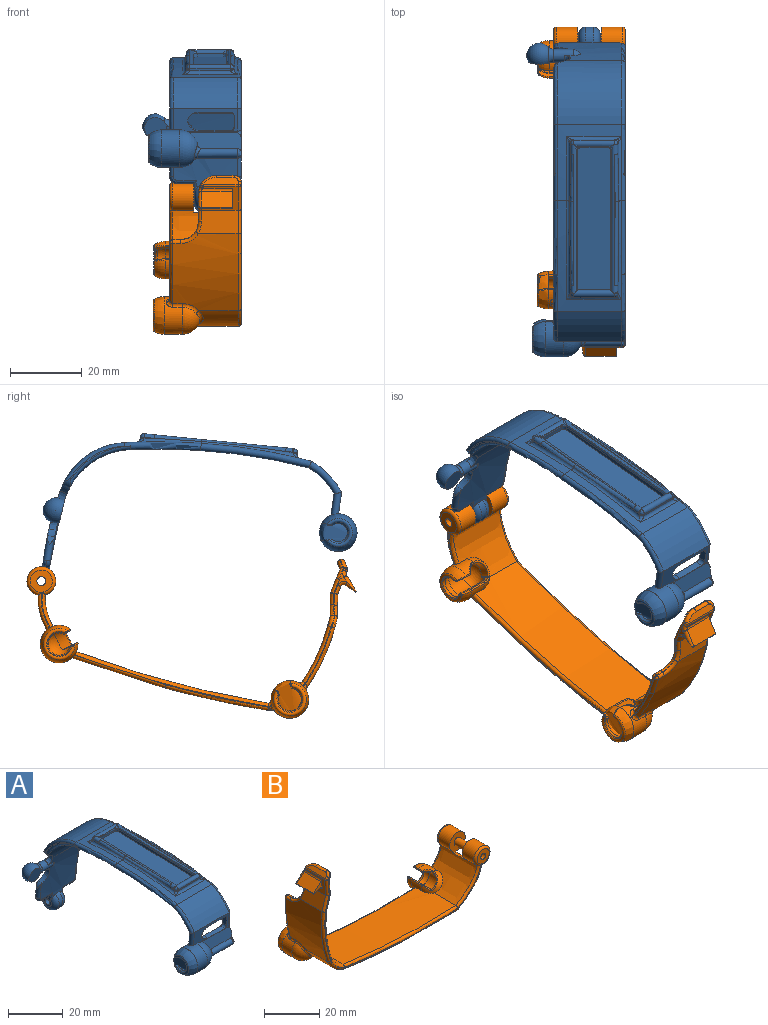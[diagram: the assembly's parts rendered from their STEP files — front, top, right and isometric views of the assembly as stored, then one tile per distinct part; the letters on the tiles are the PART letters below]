
ASSEMBLY  parts=2 mates=1
PART A: 147 faces, bbox 30.4x94.3x50.8 mm
  f0: plane 36.93x1.25mm, normal (0,-0.03,1), area 5.1mm2, adj f125,f126,f127
  f1: plane 2.82x0.31mm, normal (1,0,0), area 0.4mm2, adj f113,f123,f136
  f2: plane 2.24x0.34mm, normal (-1,0,0), area 0.3mm2, adj f112,f126,f129
  f3: torus R=90.74mm, axis (1,0,0), area 17.7mm2, adj f4,f22,f74,f76,f97
  f4: cylinder r=89.74mm len=21.05mm, axis (-1,0,0), area 314.4mm2, adj f3,f6,f13,f65,f67,f68,f75,f76
  f5: cylinder r=20mm len=18mm, axis (-1,0,0), area 420.5mm2, adj f7,f22,f23,f66,f94,f95
  f6: cylinder r=20mm len=18mm, axis (1,0,0), area 425.5mm2, adj f4,f8,f28,f64,f94,f95,f96
  f7: torus R=19mm, axis (1,0,0), area 31.9mm2, adj f5,f19,f73,f94
  f8: torus R=21mm, axis (1,0,0), area 31.6mm2, adj f6,f19,f73,f94
  f9: torus R=2mm, axis (1,0,0), area 2.1mm2, adj f10,f11,f20,f29,f60
  f10: cylinder r=1mm len=6.94mm, axis (0,0.08,-1), area 19.6mm2, adj f9,f11,f17,f18,f59,f61
  f11: plane 0.58x0.06mm, normal (1,0,0), area 0mm2, adj f9,f10,f59
  f12: plane 18.1x15.35mm, normal (1,0,0), area 6.5mm2, adj f63,f64,f65,f66
  f13: cylinder r=4mm len=8mm, axis (-1,0,0), area 46.1mm2, adj f4,f22,f83,f84
  f14: sphere r=3.75mm, area 55.4mm2, adj f35,f37,f38
  f15: cylinder r=1.3mm len=11.27mm, axis (-1,0,0), area 43.9mm2, adj f16,f20,f57,f77
  f16: cylinder r=1.8mm len=11.38mm, axis (-1,0,0), area 28.9mm2, adj f15,f21,f58,f77
  f17: plane 18.02x6.38mm, normal (0,-1,-0.08), area 48.4mm2, adj f10,f25,f30,f31,f39,f41,f42,f60
  f18: plane 18.02x6.15mm, normal (0,1,0.08), area 43.8mm2, adj f10,f21,f26,f30,f31,f39,f40,f41
  f19: plane 16.22x10.31mm, normal (-1,0,0), area 5.9mm2, adj f7,f8,f73,f94
  f20: plane 17.67x8.45mm, normal (0,-0.98,0.21), area 59.6mm2, adj f9,f15,f29,f30,f57,f60,f77
  f21: plane 15.46x6.4mm, normal (0,0.98,-0.21), area 77.7mm2, adj f16,f18,f30,f59,f77
  f22: cylinder r=91.74mm len=22.56mm, axis (-1,0,0), area 338.7mm2, adj f3,f5,f13,f65,f68,f69,f74,f75
  f23: cylinder r=192.82mm len=21.29mm, axis (-1,0,0), area 109.1mm2, adj f5,f24,f63,f73,f113,f114,f115
  f24: cylinder r=165.2mm len=31.08mm, axis (-1,0,0), area 136.2mm2, adj f23,f25,f62,f72,f110,f111,f112
  f25: cylinder r=22mm len=18mm, axis (-1,0,0), area 220.3mm2, adj f17,f24,f61,f71
  f26: cylinder r=20mm len=18mm, axis (-1,0,0), area 184mm2, adj f18,f27,f61,f71
  f27: cylinder r=163.2mm len=30.43mm, axis (-1,0,0), area 550.9mm2, adj f26,f28,f62,f72
  f28: cylinder r=190.82mm len=19.58mm, axis (-1,0,0), area 353.1mm2, adj f6,f27,f63,f73
  f29: plane 7.23x3.75mm, normal (1,0,0), area 5.1mm2, adj f9,f20,f57,f58,f59
  f30: sphere r=5.25mm, area 114.2mm2, adj f17,f18,f20,f21,f31,f51,f52,f60
  f31: cylinder r=5.25mm len=10.5mm, axis (-1,0,0), area 130.2mm2, adj f17,f18,f30,f32,f49,f50,f53,f70
  f32: revolved ~10.48x10.02mm, area 94mm2, adj f31,f45,f48,f54
  f33: cone r=3.42mm half-angle=35.3deg, axis (-1,0,0), area 10.2mm2, adj f34,f45,f46,f56
  f34: sphere r=3.75mm, area 52.2mm2, adj f33,f35,f36,f38,f46,f56
  f35: cylinder r=3.75mm len=7.5mm, axis (1,0,0), area 91.7mm2, adj f14,f34,f36,f37,f38
  f36: plane 5.15x2.64mm, normal (0,-0.04,-1), area 6.5mm2, adj f34,f35,f37,f46,f47,f48,f49
  f37: cylinder r=3.75mm len=6.95mm, axis (0,-1,0.04), area 29.1mm2, adj f14,f35,f36,f38,f49,f50,f51
  f38: plane 11.67x4.47mm, normal (0,0.04,1), area 15mm2, adj f14,f34,f35,f37,f51,f52,f53,f54
  f39: plane 2.02x0.45mm, normal (0.64,-0.06,0.77), area 0.9mm2, adj f17,f18,f80,f81
  f40: plane 8.64x2mm, normal (0,-0.08,1), area 17.4mm2, adj f18,f60,f78,f80
  f41: plane 3.64x2.26mm, normal (-1,0,0), area 7mm2, adj f17,f18,f78,f79
  f42: plane 9x1.99mm, normal (0,0.08,-1), area 18mm2, adj f17,f18,f79,f82
  f43: plane 6.03x4mm, normal (1,0,0), area 9.9mm2, adj f68,f84,f85,f86,f88
  f44: plane 6.03x4mm, normal (-1,0,0), area 9.9mm2, adj f75,f83,f85,f87,f89
  f45: torus R=3.5mm, axis (1,0,0), area 18.5mm2, adj f32,f33,f47,f55
  f46: bspline ~1.96x1.9mm, area 0.2mm2, adj f33,f34,f36,f47
  f47: bspline ~1.27x0.49mm, area 0.4mm2, adj f36,f45,f46,f48
  f48: bspline ~5.35x2.73mm, area 2.4mm2, adj f32,f36,f47,f49
  f49: cylinder r=0.3mm len=1.81mm, axis (-1,0,0), area 1.1mm2, adj f31,f36,f37,f48,f50
  f50: bspline ~4.25x2.57mm, area 2.8mm2, adj f31,f37,f49,f51
  f51: torus R=4.05mm, axis (0,-1,0.04), area 6.3mm2, adj f30,f37,f38,f50,f52
  f52: torus R=4.46mm, axis (0,0.04,1), area 2.4mm2, adj f30,f38,f51,f53
  f53: cylinder r=0.3mm len=5mm, axis (-1,0,0), area 3mm2, adj f31,f38,f52,f54
  f54: bspline ~5.37x2.69mm, area 2.3mm2, adj f32,f38,f53,f55
  f55: bspline ~1.27x0.49mm, area 0.4mm2, adj f38,f45,f54,f56
  f56: bspline ~1.99x1.88mm, area 0.2mm2, adj f33,f34,f38,f55
  f57: torus R=0.3mm, axis (1,0,0), area 2.9mm2, adj f15,f20,f29,f58
  f58: torus R=0.8mm, axis (1,0,0), area 3.2mm2, adj f16,f29,f57,f59
  f59: cylinder r=1mm len=6.55mm, axis (0,-0.21,-0.98), area 9.9mm2, adj f10,f11,f21,f29,f58
  f60: cylinder r=1mm len=14.43mm, axis (1,0,0), area 2.8mm2, adj f9,f17,f20,f30,f40,f78,f80
  f61: torus R=21mm, axis (1,0,0), area 35.3mm2, adj f10,f25,f26,f62
  f62: torus R=164.2mm, axis (1,0,0), area 97.2mm2, adj f24,f27,f61,f63
  f63: torus R=191.82mm, axis (1,0,0), area 64.3mm2, adj f12,f23,f28,f62,f64,f66
  f64: torus R=21mm, axis (1,0,0), area 38.4mm2, adj f6,f12,f63,f65
  f65: torus R=90.74mm, axis (1,0,0), area 60.4mm2, adj f4,f12,f22,f64,f66,f67,f69
  f66: torus R=19mm, axis (1,0,0), area 36.2mm2, adj f5,f12,f63,f65
  f67: bspline ~2.7x2.49mm, area 4.4mm2, adj f4,f65,f68,f69
  f68: cylinder r=1mm len=5.5mm, axis (-1,0,0), area 16.2mm2, adj f4,f22,f43,f67,f69,f86,f88
  f69: bspline ~2.5x2.45mm, area 3.7mm2, adj f22,f65,f67,f68
  f70: cylinder r=1mm len=6.86mm, axis (0,0.08,-1), area 18.8mm2, adj f17,f18,f31,f71
  f71: torus R=21mm, axis (1,0,0), area 35.3mm2, adj f25,f26,f70,f72
  f72: torus R=164.2mm, axis (1,0,0), area 97.2mm2, adj f24,f27,f71,f73
  f73: torus R=191.82mm, axis (1,0,0), area 64.3mm2, adj f7,f8,f19,f23,f28,f72
  f74: bspline ~2.5x2.12mm, area 3.7mm2, adj f3,f22,f75,f76
  f75: cylinder r=1mm len=5.5mm, axis (1,0,0), area 16.2mm2, adj f4,f22,f44,f74,f76,f87,f89
  f76: bspline ~2.7x2.49mm, area 4.4mm2, adj f3,f4,f74,f75
  f77: bspline ~3.87x3.87mm, area 6.3mm2, adj f15,f16,f20,f21,f30
  f78: cylinder r=1mm len=2.08mm, axis (0,-1,-0.08), area 3.1mm2, adj f17,f18,f40,f41,f60
  f79: cylinder r=1mm len=2.07mm, axis (0,1,0.08), area 3.1mm2, adj f17,f18,f41,f42
  f80: cylinder r=3mm len=2.06mm, axis (0,1,0.08), area 4.2mm2, adj f17,f18,f39,f40,f60
  f81: cylinder r=3mm len=2.14mm, axis (0,1,0.08), area 4.5mm2, adj f17,f18,f39,f82
  f82: cylinder r=3mm len=2.97mm, axis (0,-1,-0.08), area 8.6mm2, adj f17,f18,f42,f81
  f83: torus R=2mm, axis (-1,0,0), area 58.5mm2, adj f4,f13,f22,f44,f87,f89
  f84: torus R=2mm, axis (1,0,0), area 58.5mm2, adj f4,f13,f22,f43,f86,f88
  f85: cylinder r=1.25mm len=6mm, axis (-1,0,0), area 47.1mm2, adj f43,f44
  f86: torus R=90.24mm, axis (1,0,0), area 1.9mm2, adj f4,f43,f68,f84
  f87: torus R=90.24mm, axis (-1,0,0), area 1.9mm2, adj f4,f44,f75,f83
  f88: torus R=91.24mm, axis (1,0,0), area 1.5mm2, adj f22,f43,f68,f84
  f89: torus R=91.24mm, axis (-1,0,0), area 1.5mm2, adj f22,f44,f75,f83
  f90: revolved ~3.38x2.08mm, area 7mm2, adj f22,f91
  f91: cylinder r=1.8mm len=6.5mm, axis (1,0,0), area 51.9mm2, adj f4,f22,f90,f92,f96,f98,f144,f145
  f92: revolved ~1.93x0.55mm, area 0mm2, adj f4,f91
  f93: sphere r=3.5mm, area 99.9mm2, adj f145,f146
  f94: torus R=9.76mm, axis (1,0,0), area 4.5mm2, adj f5,f6,f7,f8,f19,f95
  f95: torus R=1.3mm, axis (1,0,0), area 6.8mm2, adj f5,f6,f22,f94,f96
  f96: revolved ~5.43x4.87mm, area 10.5mm2, adj f4,f6,f22,f91,f95
  f97: torus R=9.76mm, axis (1,0,0), area 4.1mm2, adj f3,f4,f22,f99
  f98: revolved ~6.43x4.21mm, area 11.4mm2, adj f4,f22,f91,f99
  f99: torus R=1.3mm, axis (1,0,0), area 6.6mm2, adj f4,f22,f97,f98
  f100: plane 11.32x0.55mm, normal (0,1,0.03), area 6.3mm2, adj f115,f124,f135,f136,f141,f142
  f101: plane 7.29x1mm, normal (0,-1,-0.03), area 7.3mm2, adj f109,f124,f133,f139
  f102: plane 39.01x2.32mm, normal (-1,0,0), area 39mm2, adj f106,f109,f123,f133
  f103: plane 39.01x2.32mm, normal (1,0,0), area 39mm2, adj f106,f109,f126,f139
  f104: plane 2.24x0.34mm, normal (1,0,0), area 0.3mm2, adj f111,f119,f123
  f105: plane 2.82x0.31mm, normal (-1,0,0), area 0.4mm2, adj f114,f126,f141
  f106: plane 9.29x1mm, normal (0,1,0.03), area 9.3mm2, adj f102,f103,f109,f116
  f107: plane 11.33x0.52mm, normal (0,-1,-0.03), area 5.9mm2, adj f110,f116,f118,f119,f129,f130
  f108: plane 36.93x1.25mm, normal (0,-0.03,1), area 5.1mm2, adj f120,f121,f123
  f109: plane 39.98x9.29mm, normal (0,-0.03,1), area 371.3mm2, adj f101,f102,f103,f106,f133,f139
  f110: cylinder r=1mm len=15.29mm, axis (-1,0,0), area 19.1mm2, adj f24,f107,f117,f131
  f111: torus R=166.2mm, axis (1,0,0), area 32.9mm2, adj f24,f104,f113,f117,f118,f121
  f112: torus R=166.2mm, axis (1,0,0), area 32.9mm2, adj f2,f24,f114,f127,f130,f131
  f113: torus R=193.82mm, axis (1,0,0), area 23.2mm2, adj f1,f23,f111,f120,f134,f135
  f114: torus R=193.82mm, axis (1,0,0), area 23.2mm2, adj f23,f105,f112,f125,f142,f143
  f115: cylinder r=1mm len=15.29mm, axis (-1,0,0), area 19.2mm2, adj f23,f100,f134,f143
  f116: cylinder r=1mm len=11.29mm, axis (-1,0,0), area 33.9mm2, adj f106,f107,f122,f123,f126,f128
  f117: bspline ~2x1.81mm, area 1.1mm2, adj f110,f111,f118
  f118: bspline ~1.15x1.06mm, area 0.3mm2, adj f107,f111,f117,f119
  f119: cylinder r=1mm len=1.01mm, axis (0,0.03,-1), area 0.4mm2, adj f104,f107,f118,f122
  f120: bspline ~18.57x1.17mm, area 17.2mm2, adj f108,f113,f121,f123
  f121: bspline ~28.71x2.17mm, area 28.3mm2, adj f108,f111,f120,f123
  f122: sphere r=1mm, area 2.2mm2, adj f116,f119,f123
  f123: cylinder r=1mm len=42.01mm, axis (0,-1,-0.03), area 71.6mm2, adj f1,f102,f104,f108,f116,f120,f121,f122
  f124: cylinder r=1mm len=11.29mm, axis (1,0,0), area 31.5mm2, adj f100,f101,f132,f137,f138,f140
  f125: bspline ~18.57x1.17mm, area 17.2mm2, adj f0,f114,f126,f127
  f126: cylinder r=1mm len=42.01mm, axis (0,1,0.03), area 71.6mm2, adj f0,f2,f103,f105,f116,f125,f127,f128
  f127: bspline ~28.71x2.17mm, area 28.3mm2, adj f0,f112,f125,f126
  f128: sphere r=1mm, area 2.2mm2, adj f116,f126,f129
  f129: cylinder r=1mm len=1.01mm, axis (0,-0.03,1), area 0.4mm2, adj f2,f107,f128,f130
  f130: bspline ~1.15x1.06mm, area 0.3mm2, adj f107,f112,f129,f131
  f131: bspline ~2x1.81mm, area 1.1mm2, adj f110,f112,f130
  f132: bspline ~2x1.97mm, area 1.1mm2, adj f123,f124,f133
  f133: cylinder r=1mm len=1.03mm, axis (0,0.03,-1), area 1.6mm2, adj f101,f102,f109,f132
  f134: bspline ~2x1.9mm, area 1.1mm2, adj f113,f115,f135
  f135: bspline ~1.25x1.07mm, area 0.3mm2, adj f100,f113,f134,f136
  f136: cylinder r=1mm len=1.01mm, axis (0,-0.03,1), area 0.5mm2, adj f1,f100,f135,f137
  f137: sphere r=1mm, area 1.6mm2, adj f123,f124,f136
  f138: bspline ~2x1.97mm, area 1.1mm2, adj f124,f126,f139
  f139: cylinder r=1mm len=1.03mm, axis (0,-0.03,1), area 1.6mm2, adj f101,f103,f109,f138
  f140: sphere r=1mm, area 1.6mm2, adj f124,f126,f141
  f141: cylinder r=1mm len=1.01mm, axis (0,0.03,-1), area 0.5mm2, adj f100,f105,f140,f142
  f142: bspline ~1.25x1.07mm, area 0.3mm2, adj f100,f114,f141,f143
  f143: bspline ~2x1.9mm, area 1.1mm2, adj f114,f115,f142
  f144: plane 0.83x0.15mm, normal (-1,0,0), area 0mm2, adj f91,f145
  f145: plane 9x7.97mm, normal (0,-0.99,-0.17), area 29.5mm2, adj f91,f93,f144,f146
  f146: torus R=3.8mm, axis (-1,0,0), area 17.1mm2, adj f91,f93,f145
PART B: 197 faces, bbox 91x25.8x52.7 mm
  f0: cylinder r=4mm len=8mm, axis (0,1,0), area 135.1mm2, adj f7,f8,f59,f175
  f1: plane 4.47x0.17mm, normal (0,1,0), area 0.4mm2, adj f4,f10,f107
  f2: bspline ~11.01x6.63mm, area 14.7mm2, adj f5,f7,f60,f107
  f3: bspline ~11.4x6.92mm, area 13.7mm2, adj f5,f8,f60,f107
  f4: torus R=284.06mm, axis (0,-1,0), area 78.1mm2, adj f1,f9,f10,f18,f28,f107,f191
  f5: plane 14.87x9.43mm, normal (0,1,0), area 27.4mm2, adj f2,f3,f60,f107,f177
  f6: plane 27.53x18.26mm, normal (0,0,-1), area 498.8mm2, adj f10,f11,f35,f69,f106,f107
  f7: extruded ~18.2x13.62mm, area 276.8mm2, adj f0,f2,f11,f36,f64,f106,f107,f173
  f8: extruded ~18.2x12.35mm, area 249.7mm2, adj f0,f3,f9,f36,f63,f107,f111,f174
  f9: cylinder r=283.16mm len=57.7mm, axis (0,1,0), area 1042.2mm2, adj f4,f8,f24,f66,f107,f111,f193,f195
  f10: cylinder r=0.9mm len=27.21mm, axis (1,0,0), area 37.4mm2, adj f1,f4,f6,f28,f72,f107
  f11: cylinder r=285.16mm len=13.84mm, axis (0,1,0), area 24.4mm2, adj f6,f7,f67,f106
  f12: cylinder r=5.25mm len=10.5mm, axis (0,1,0), area 106.1mm2, adj f15,f16,f101,f142,f145,f150,f180,f182
  f13: sphere r=3.75mm, area 36mm2, adj f17,f105,f131,f136
  f14: cone r=3mm half-angle=42.1deg, axis (0,1,0), area 7.1mm2, adj f129,f130,f131,f132
  f15: revolved ~10.49x10.49mm, area 76.8mm2, adj f12,f130,f140,f151
  f16: sphere r=5.25mm, area 20mm2, adj f12,f146,f148,f149,f194,f195,f196
  f17: cylinder r=3.75mm len=7.5mm, axis (0,-1,0), area 90.7mm2, adj f13,f102,f105,f138,f139
  f18: torus R=12.41mm, axis (0,-1,0), area 0mm2, adj f4,f28,f189
  f19: torus R=52.54mm, axis (0,-1,0), area 24.3mm2, adj f25,f26,f75,f186
  f20: torus R=12.61mm, axis (0,-1,0), area 0.9mm2, adj f23,f28,f72,f185
  f21: torus R=52.74mm, axis (0,-1,0), area 25.6mm2, adj f22,f26,f79,f182
  f22: cylinder r=53.64mm len=23.61mm, axis (0,1,0), area 404.9mm2, adj f21,f23,f34,f76,f83,f86,f179,f180
  f23: cylinder r=13.51mm len=18.2mm, axis (0,1,0), area 121.4mm2, adj f20,f22,f35,f74,f181,f183
  f24: cylinder r=11.51mm len=13.74mm, axis (0,1,0), area 91.6mm2, adj f9,f25,f62,f194,f196
  f25: cylinder r=51.64mm len=22.47mm, axis (0,1,0), area 381mm2, adj f19,f24,f37,f58,f68,f70,f73,f188
  f26: plane 17.37x2.25mm, normal (0,1,0), area 3.5mm2, adj f19,f21,f77,f184
  f27: plane 46.76x44.23mm, normal (0,-1,0), area 15.9mm2, adj f47,f49,f51,f55,f58,f62,f66,f69
  f28: plane 34.37x3.13mm, normal (0,1,0), area 6.3mm2, adj f4,f10,f18,f20,f72,f187
  f29: plane 8.6x3.86mm, normal (-0.66,0,0.75), area 44.2mm2, adj f30,f42,f93,f99,f100
  f30: plane 9.13x0.33mm, normal (-0.96,0,-0.29), area 2.8mm2, adj f29,f31,f42,f97,f100
  f31: plane 8.6x3.23mm, normal (0.29,0,-0.96), area 29mm2, adj f30,f42,f94,f97
  f32: plane 22.75x19.9mm, normal (0,-1,0), area 29.8mm2, adj f59,f63,f64,f66,f67,f69,f177
  f33: plane 10.2x7.12mm, normal (-1,0,-0.07), area 35.8mm2, adj f34,f42,f82,f88,f92,f93,f94,f95
  f34: plane 11.13x6.16mm, normal (-0.95,0,0.3), area 66.7mm2, adj f22,f33,f78,f86,f89,f91
  f35: cylinder r=285.16mm len=29.4mm, axis (0,1,0), area 538mm2, adj f6,f23,f71,f72
  f36: cylinder r=4mm len=8mm, axis (0,1,0), area 135.1mm2, adj f7,f8,f60,f174
  f37: plane 11.06x6.16mm, normal (0.95,0,-0.3), area 66.7mm2, adj f25,f55,f56,f65,f68
  f38: plane 10.25x7.03mm, normal (1,0,0.07), area 70.1mm2, adj f39,f51,f52,f54,f56,f57
  f39: plane 9.32x1.21mm, normal (0.77,0,-0.63), area 12.8mm2, adj f38,f48,f49,f50,f52
  f40: plane 5x0.15mm, normal (0.63,0,0.77), area 1mm2, adj f45,f47,f50,f84
  f41: plane 9.62x1.55mm, normal (-0.77,0,0.63), area 17mm2, adj f80,f81,f84,f87,f88
  f42: plane 4.47x4.43mm, normal (0,-1,0), area 7mm2, adj f29,f30,f31,f33,f93,f94
  f43: plane 2.1x0.2mm, normal (-0.07,0,1), area 0.4mm2, adj f46,f73,f77,f83
  f44: plane 8.18x2.63mm, normal (0,1,0), area 3.3mm2, adj f45,f46,f57,f65,f91,f95,f98,f100
  f45: cylinder r=5mm len=5.3mm, axis (-0.77,0,0.63), area 2.7mm2, adj f40,f44,f52,f54,f87,f92,f96,f99
  f46: cylinder r=5mm len=5.12mm, axis (1,0,0.07), area 1.6mm2, adj f43,f44,f68,f70,f86,f89
  f47: cylinder r=2mm len=2mm, axis (0.77,0,-0.63), area 0.6mm2, adj f27,f40,f48,f80
  f48: torus R=1.1mm, axis (-0.77,0,0.63), area 3.7mm2, adj f39,f47,f49,f50
  f49: cylinder r=0.9mm len=1.22mm, axis (-0.63,0,-0.77), area 0.9mm2, adj f27,f39,f48,f51
  f50: cylinder r=0.9mm len=5mm, axis (0,-1,0), area 7.1mm2, adj f39,f40,f48,f52
  f51: cylinder r=0.9mm len=7.31mm, axis (0.07,0,-1), area 10mm2, adj f27,f38,f49,f53
  f52: torus R=4.1mm, axis (-0.77,0,0.63), area 6.4mm2, adj f38,f39,f45,f50,f54
  f53: sphere r=0.9mm, area 0.3mm2, adj f51,f55,f56
  f54: bspline ~5.17x1.9mm, area 4mm2, adj f38,f45,f52,f57
  f55: cylinder r=0.9mm len=6.51mm, axis (-0.3,0,-0.95), area 9.2mm2, adj f27,f37,f53,f58
  f56: cylinder r=0.9mm len=10.2mm, axis (0,1,0), area 3.5mm2, adj f37,f38,f53,f61
  f57: cylinder r=0.9mm len=4.32mm, axis (-0.07,0,1), area 6mm2, adj f38,f44,f54,f61
  f58: torus R=52.54mm, axis (0,-1,0), area 32.5mm2, adj f25,f27,f55,f62
  f59: torus R=3.1mm, axis (0,-1,0), area 31.1mm2, adj f0,f32,f63,f64
  f60: torus R=3.1mm, axis (0,-1,0), area 31.1mm2, adj f2,f3,f5,f36
  f61: sphere r=0.9mm, area 0.2mm2, adj f56,f57,f65
  f62: torus R=12.41mm, axis (0,-1,0), area 12.9mm2, adj f24,f27,f58,f66
  f63: bspline ~15.44x12.58mm, area 24.9mm2, adj f8,f32,f59,f66
  f64: bspline ~16.73x14.83mm, area 26.7mm2, adj f7,f32,f59,f67
  f65: cylinder r=0.9mm len=3.27mm, axis (0.3,0,0.95), area 4.4mm2, adj f37,f44,f61,f68
  f66: torus R=284.06mm, axis (0,-1,0), area 81.4mm2, adj f9,f27,f32,f62,f63,f69
  f67: torus R=284.26mm, axis (0,-1,0), area 2.6mm2, adj f11,f32,f64,f69
  f68: bspline ~4.39x2.28mm, area 4.8mm2, adj f25,f37,f46,f65,f70
  f69: cylinder r=0.9mm len=27.46mm, axis (-1,0,0), area 38mm2, adj f6,f27,f32,f66,f67,f71
  f70: bspline ~6.86x4.28mm, area 8.1mm2, adj f25,f46,f68,f73
  f71: torus R=284.26mm, axis (0,-1,0), area 41.7mm2, adj f27,f35,f69,f74
  f72: torus R=284.26mm, axis (0,-1,0), area 41.7mm2, adj f10,f20,f28,f35
  f73: cylinder r=0.9mm len=2.1mm, axis (0,1,0), area 3.2mm2, adj f25,f43,f70,f75
  f74: torus R=12.61mm, axis (0,-1,0), area 14.6mm2, adj f23,f27,f71,f76
  f75: sphere r=0.9mm, area 1.4mm2, adj f19,f73,f77
  f76: torus R=52.74mm, axis (0,-1,0), area 33.6mm2, adj f22,f27,f74,f78
  f77: cylinder r=0.9mm len=0.91mm, axis (-1,0,-0.07), area 0.3mm2, adj f26,f43,f75,f79
  f78: cylinder r=0.9mm len=6.58mm, axis (0.3,0,0.95), area 9.2mm2, adj f27,f34,f76,f82
  f79: sphere r=0.9mm, area 0.8mm2, adj f21,f77,f83
  f80: torus R=1.1mm, axis (-0.77,0,0.63), area 3.7mm2, adj f41,f47,f81,f84
  f81: cylinder r=0.9mm len=1.27mm, axis (0.63,0,0.77), area 1.3mm2, adj f27,f41,f80,f85
  f82: cylinder r=0.9mm len=7.35mm, axis (-0.07,0,1), area 10.2mm2, adj f27,f33,f78,f85
  f83: cylinder r=0.9mm len=2.1mm, axis (0,1,0), area 2.7mm2, adj f22,f43,f79,f86
  f84: cylinder r=0.9mm len=5mm, axis (0,1,0), area 7.1mm2, adj f40,f41,f80,f87
  f85: sphere r=0.9mm, area 0.5mm2, adj f81,f82,f88
  f86: bspline ~6.86x4.27mm, area 7.2mm2, adj f22,f34,f46,f83,f89
  f87: torus R=4.1mm, axis (-0.77,0,0.63), area 6.8mm2, adj f41,f45,f84,f90
  f88: cylinder r=0.9mm len=9.62mm, axis (0,1,0), area 6.6mm2, adj f33,f41,f85,f90
  f89: bspline ~4.16x2.16mm, area 4.3mm2, adj f34,f46,f86,f91
  f90: sphere r=0.9mm, area 0.6mm2, adj f87,f88,f92
  f91: cylinder r=0.9mm len=3.31mm, axis (-0.3,0,-0.95), area 4.4mm2, adj f34,f44,f89,f95
  f92: bspline ~2.44x1.83mm, area 1.1mm2, adj f33,f45,f90,f96
  f93: cylinder r=0.9mm len=8.6mm, axis (0,-1,0), area 7mm2, adj f29,f33,f42,f96
  f94: cylinder r=0.9mm len=8.6mm, axis (0,-1,0), area 13.8mm2, adj f31,f33,f42,f98
  f95: cylinder r=0.9mm len=2.52mm, axis (0.07,0,-1), area 3.4mm2, adj f33,f44,f91,f98
  f96: bspline ~2.2x1.63mm, area 2.1mm2, adj f45,f92,f93,f99
  f97: cylinder r=0.9mm len=3.48mm, axis (0.96,0,0.29), area 3.2mm2, adj f30,f31,f98,f100
  f98: torus R=1.8mm, axis (0,-1,0), area 3.1mm2, adj f44,f94,f95,f97,f100
  f99: bspline ~1.9x1.85mm, area 0.3mm2, adj f29,f45,f96,f100
  f100: cylinder r=0.9mm len=4.39mm, axis (-0.75,0,-0.66), area 5.7mm2, adj f29,f30,f44,f97,f98,f99
  f101: sphere r=5.25mm, area 65mm2, adj f12,f179,f181
  f102: sphere r=3.75mm, area 55.1mm2, adj f17,f104,f105,f147
  f103: plane 4.39x1.24mm, normal (0.71,0,-0.71), area 4.5mm2, adj f132,f134,f136,f137,f138,f140,f142,f143
  f104: cylinder r=3.75mm len=7.02mm, axis (-0.71,0,-0.71), area 29.2mm2, adj f102,f139,f143,f145,f146,f147
  f105: plane 11.04x2.58mm, normal (-0.71,0,0.71), area 13.5mm2, adj f13,f17,f102,f129,f131,f147,f149,f150
  f106: sphere r=5.25mm, area 79.4mm2, adj f6,f7,f11,f107
  f107: cylinder r=5.25mm len=10.5mm, axis (0,1,0), area 120.2mm2, adj f1,f2,f3,f4,f5,f6,f7,f8
  f108: sphere r=3.75mm, area 38.5mm2, adj f112,f121,f126,f157
  f109: cone r=2.84mm half-angle=49.9deg, axis (0,1,0), area 4.9mm2, adj f125,f126,f127,f128
  f110: torus R=0mm, axis (0,1,0), area 79.6mm2, adj f107,f127,f160,f170
  f111: sphere r=5.25mm, area 29.8mm2, adj f8,f9,f107,f164,f166,f167
  f112: cylinder r=3.75mm len=7.5mm, axis (0,-1,0), area 90.8mm2, adj f108,f113,f114,f120,f121,f122,f159
  f113: sphere r=3.75mm, area 2mm2, adj f112,f115,f116,f123
  f114: sphere r=3.75mm, area 3.5mm2, adj f112,f117,f118,f119
  f115: extruded ~3.09x0.26mm, area 0.5mm2, adj f113,f116,f120
  f116: cylinder r=3.42mm len=3.09mm, axis (0,-1,0), area 3.8mm2, adj f113,f115,f120,f123
  f117: cylinder r=283.16mm len=3.09mm, axis (0,1,0), area 0.5mm2, adj f114,f119,f120
  f118: cylinder r=285.16mm len=3.09mm, axis (0,1,0), area 0.7mm2, adj f114,f119,f120
  f119: cylinder r=3.42mm len=3.09mm, axis (0,-1,0), area 6.9mm2, adj f114,f117,f118,f120
  f120: sphere r=3.75mm, area 47.8mm2, adj f112,f115,f116,f117,f118,f119,f122,f161
  f121: plane 4.81x1.66mm, normal (-0.71,0,-0.71), area 5.4mm2, adj f108,f112,f122,f126,f128,f169,f170,f171
  f122: cylinder r=3.75mm len=7.06mm, axis (0.71,0,-0.71), area 28.8mm2, adj f112,f120,f121,f123,f165,f167,f168,f169
  f123: plane 3.09x0.24mm, normal (-0.71,0,0.71), area 0.7mm2, adj f113,f116,f122
  f124: plane 10.87x2.08mm, normal (0.71,0,0.71), area 11.7mm2, adj f125,f155,f157,f158,f159,f160,f161,f162
  f125: bspline ~2.03x1.97mm, area 0.5mm2, adj f109,f124,f154,f156
  f126: torus R=3.66mm, axis (0,-1,0), area 13.1mm2, adj f108,f109,f121,f128,f154,f155
  f127: torus R=3.89mm, axis (0,-1,0), area 20.3mm2, adj f109,f110,f156,f158,f171,f172
  f128: bspline ~2.03x1.97mm, area 0.5mm2, adj f109,f121,f126,f172
  f129: bspline ~2.32x1.97mm, area 0.5mm2, adj f14,f105,f131,f153
  f130: torus R=4.04mm, axis (0,-1,0), area 24.3mm2, adj f14,f15,f135,f137,f152,f153
  f131: torus R=3.76mm, axis (0,-1,0), area 11.9mm2, adj f13,f14,f105,f129,f133,f134
  f132: bspline ~1.97x1.68mm, area 0.5mm2, adj f14,f103,f133,f135
  f133: bspline ~0.7x0.4mm, area 0.1mm2, adj f131,f132,f134
  f134: bspline ~0.33x0.31mm, area 0mm2, adj f103,f131,f133,f136
  f135: bspline ~0.87x0.61mm, area 0.2mm2, adj f130,f132,f137
  f136: torus R=3.4mm, axis (0.71,0,-0.71), area 0.6mm2, adj f13,f103,f134,f138
  f137: bspline ~0.74x0.7mm, area 0.2mm2, adj f103,f130,f135,f140
  f138: cylinder r=0.3mm len=1.6mm, axis (0,-1,0), area 0.5mm2, adj f17,f103,f136,f141
  f139: bspline ~4.05x3.63mm, area 0.6mm2, adj f17,f104,f141
  f140: bspline ~4.38x1.11mm, area 1.8mm2, adj f15,f103,f137,f142
  f141: sphere r=0.3mm, area 0.1mm2, adj f138,f139,f143
  f142: cylinder r=0.3mm len=1.6mm, axis (0,1,0), area 1mm2, adj f12,f103,f140,f144
  f143: cylinder r=0.3mm len=0.83mm, axis (-0.71,0,-0.71), area 0.3mm2, adj f103,f104,f141,f144
  f144: sphere r=0.3mm, area 0.1mm2, adj f142,f143,f145
  f145: bspline ~4.25x3.03mm, area 2.8mm2, adj f12,f104,f144,f146,f190
  f146: torus R=4.05mm, axis (-0.71,0,-0.71), area 6.2mm2, adj f16,f104,f145,f148,f192
  f147: cylinder r=0.3mm len=2.39mm, axis (-0.71,0,-0.71), area 0.8mm2, adj f102,f104,f105,f148
  f148: bspline ~0.95x0.88mm, area 0.4mm2, adj f16,f146,f147,f149
  f149: torus R=4.43mm, axis (0.71,0,-0.71), area 2.2mm2, adj f16,f105,f148,f150
  f150: cylinder r=0.3mm len=5mm, axis (0,1,0), area 3mm2, adj f12,f105,f149,f151
  f151: bspline ~5.03x1.45mm, area 1.8mm2, adj f15,f105,f150,f152
  f152: bspline ~0.74x0.7mm, area 0.2mm2, adj f105,f130,f151,f153
  f153: bspline ~0.87x0.61mm, area 0.2mm2, adj f129,f130,f152
  f154: bspline ~0.72x0.38mm, area 0.1mm2, adj f125,f126,f155
  f155: bspline ~0.33x0.29mm, area 0mm2, adj f124,f126,f154,f157
  f156: bspline ~0.96x0.65mm, area 0.2mm2, adj f125,f127,f158
  f157: torus R=3.4mm, axis (-0.71,0,-0.71), area 0.7mm2, adj f108,f124,f155,f159
  f158: bspline ~0.64x0.61mm, area 0.2mm2, adj f124,f127,f156,f160
  f159: cylinder r=0.3mm len=5mm, axis (0,-1,0), area 1.5mm2, adj f112,f124,f157,f161
  f160: bspline ~4.84x1.62mm, area 1.9mm2, adj f110,f124,f158,f162
  f161: torus R=3.4mm, axis (-0.71,0,-0.71), area 1.1mm2, adj f120,f124,f159,f163
  f162: cylinder r=0.3mm len=5mm, axis (0,1,0), area 3mm2, adj f107,f124,f160,f164
  f163: bspline ~1.29x1.05mm, area 0.1mm2, adj f120,f161,f165
  f164: torus R=4.43mm, axis (-0.71,0,-0.71), area 2.2mm2, adj f111,f124,f162,f166
  f165: cylinder r=0.3mm len=2.39mm, axis (0.71,0,-0.71), area 0.7mm2, adj f122,f124,f163,f166
  f166: bspline ~0.89x0.89mm, area 0.4mm2, adj f111,f164,f165,f167
  f167: torus R=4.05mm, axis (0.71,0,-0.71), area 6.2mm2, adj f111,f122,f166,f168
  f168: bspline ~4.43x3.39mm, area 2.8mm2, adj f107,f122,f167,f169
  f169: cylinder r=0.3mm len=1.78mm, axis (0,1,0), area 1.1mm2, adj f107,f121,f122,f168,f170
  f170: bspline ~4.84x1.62mm, area 1.9mm2, adj f110,f121,f169,f171
  f171: bspline ~0.64x0.61mm, area 0.2mm2, adj f121,f127,f170,f172
  f172: bspline ~0.96x0.65mm, area 0.2mm2, adj f127,f128,f171
  f173: cylinder r=0.25mm len=6.5mm, axis (0,-1,0), area 0.4mm2, adj f7,f174,f175,f176
  f174: plane 8.46x8mm, normal (0,-1,0), area 42.5mm2, adj f7,f8,f36,f173,f176,f178
  f175: plane 8.46x8mm, normal (0,1,0), area 42.5mm2, adj f0,f7,f8,f173,f176,f178
  f176: plane 6.5x1.82mm, normal (0.35,0,0.94), area 12.6mm2, adj f8,f173,f174,f175
  f177: cylinder r=1.25mm len=20mm, axis (0,-1,0), area 157.1mm2, adj f5,f32
  f178: cylinder r=1.65mm len=6.5mm, axis (0,-1,0), area 67.4mm2, adj f174,f175
  f179: bspline ~6.08x3.27mm, area 5.4mm2, adj f22,f101,f180,f181
  f180: cylinder r=1mm len=2.6mm, axis (0,-1,0), area 2.8mm2, adj f12,f22,f179,f182
  f181: bspline ~7.13x7.08mm, area 13.9mm2, adj f22,f23,f101,f179,f183
  f182: bspline ~2.29x2.03mm, area 2.6mm2, adj f12,f21,f180,f184
  f183: cylinder r=1mm len=2.6mm, axis (0,1,0), area 2.6mm2, adj f12,f23,f181,f185
  f184: torus R=6.25mm, axis (0,-1,0), area 0.3mm2, adj f12,f26,f182,f186
  f185: bspline ~2.28x2.26mm, area 2.6mm2, adj f12,f20,f183,f187
  f186: bspline ~2.32x2.13mm, area 2.8mm2, adj f12,f19,f184,f188
  f187: torus R=6.25mm, axis (0,-1,0), area 0.3mm2, adj f12,f28,f185,f189
  f188: cylinder r=1mm len=1.74mm, axis (0,1,0), area 2.5mm2, adj f12,f25,f186,f190
  f189: bspline ~1.22x1.06mm, area 0mm2, adj f12,f18,f187,f191
  f190: bspline ~1.24x1.14mm, area 1.2mm2, adj f25,f145,f188,f192
  f191: bspline ~1.96x1.9mm, area 2.5mm2, adj f4,f12,f189,f193
  f192: bspline ~2.94x1.22mm, area 2.5mm2, adj f25,f146,f190,f194
  f193: cylinder r=1mm len=2.6mm, axis (0,-1,0), area 3.2mm2, adj f9,f12,f191,f195
  f194: bspline ~5.25x4.16mm, area 5.4mm2, adj f16,f24,f25,f192,f196
  f195: bspline ~2.65x1.28mm, area 2.2mm2, adj f9,f16,f193,f196
  f196: bspline ~6.65x6.37mm, area 12.8mm2, adj f16,f24,f194,f195
PLACE A rot(axis=(1,0,0),3.8deg) t=(7.6,42.73,35.64)mm
PLACE B rot(axis=(0.15,-0.15,0.98),91.4deg) t=(-69.4,55.87,27.5)mm fixed
MATE revolute A.f13 <-> B.f0  axis (-1,0,0) through (-62.4,126.07,54.02)mm
